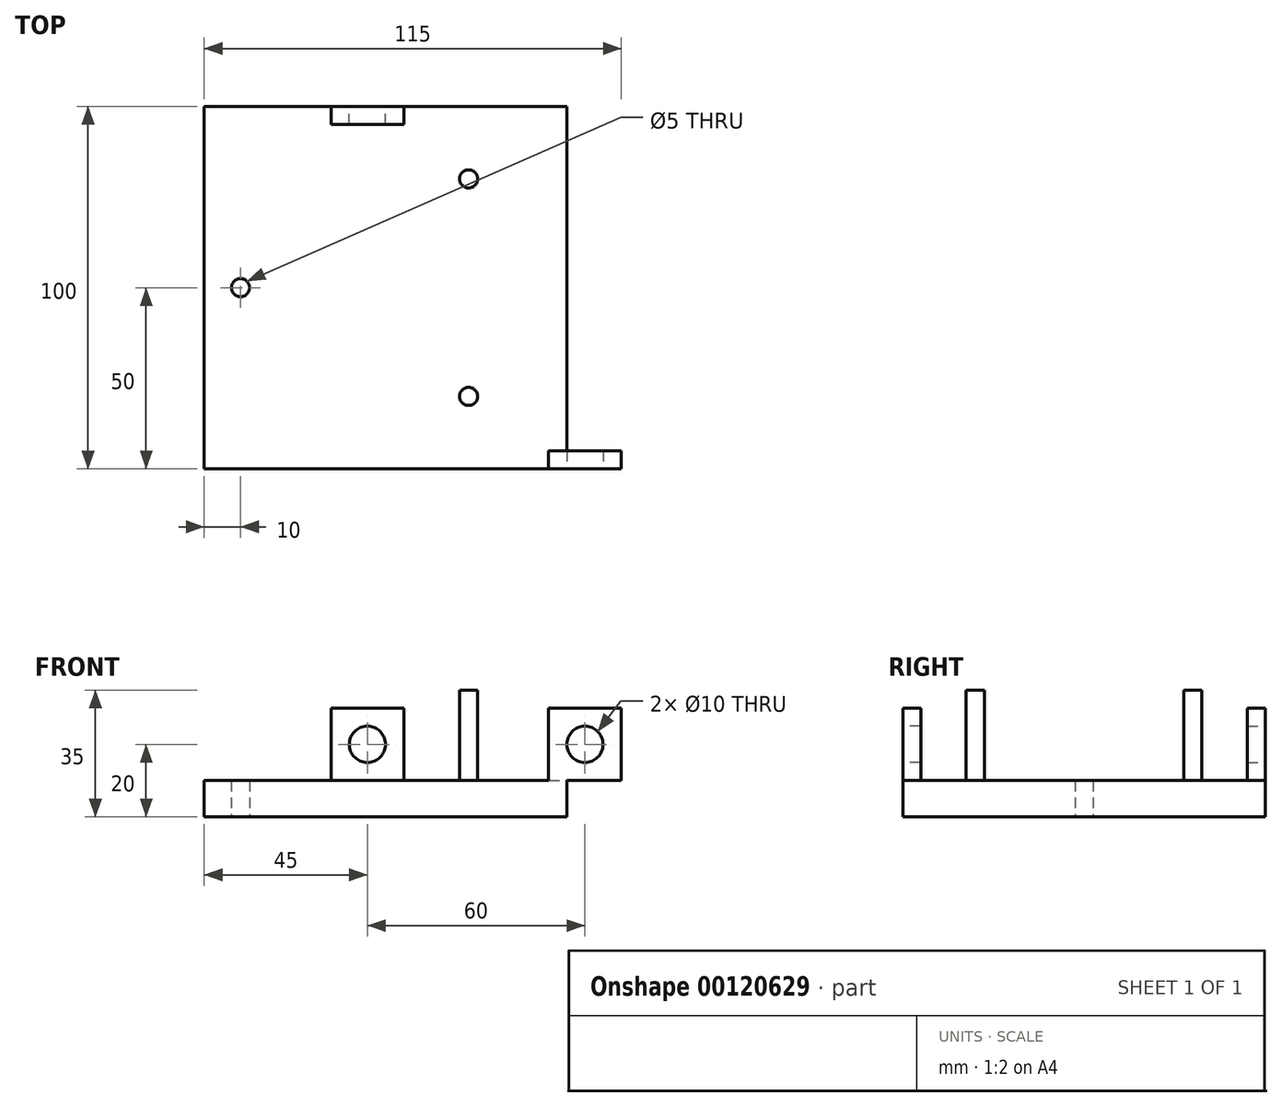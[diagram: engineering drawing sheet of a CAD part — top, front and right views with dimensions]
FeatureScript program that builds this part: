
annotation { "Feature Type Name" : "Feature", "Feature Type Description" : "" }
export const myFeature = defineFeature(function(context is Context, id is Id, definition is map)
    precondition{}
    {
        {
            var Q0;
            Q0=qCreatedBy(makeId("Top.planeOp"),FACE);
            var sketch = newSketch(context, id + "F0", { "sketchPlane" : qUnion([Q0])});
            skLineSegment(sketch, "E0.bottom", {"start": v(0, 100) * mm, "end": v(100, 100) * mm});
            skLineSegment(sketch, "E0.top", {"start": v(0, 0) * mm, "end": v(100, 0) * mm});
            skLineSegment(sketch, "E0.left", {"start": v(0, 100) * mm, "end": v(0, 0) * mm});
            skLineSegment(sketch, "E0.right", {"start": v(100, 100) * mm, "end": v(100, 0) * mm});
            skCircle(sketch, "E1", {"center": v(10, 50) * mm, "radius": 2.5 * mm});
            skSolve(sketch);
        }
        {
            var Q0;
            Q0=makeQuery(id+"F0.imprint","IMPRINT",FACE,{"disambiguationData":[TD([[makeQuery(id+"F0.imprint","IMPRINT",EDGE,{"derivedFrom":sQuery(id+"F0.wireOp",EDGE,"E0.bottom")}),-1.0]])]});
            extrude(context, id + "F1", {"entities" : qUnion([Q0]), "depth" : 10 * mm});
        }
        {
            var Q0;
            Q0=makeQuery(id+"F1.opExtrude","CAP_FACE",FACE,{"disambiguationData":[OSD([sQuery(id+"F0.wireOp",EDGE,"E0.bottom"),sQuery(id+"F0.wireOp",EDGE,"E0.top"),sQuery(id+"F0.wireOp",EDGE,"E0.left"),sQuery(id+"F0.wireOp",EDGE,"E0.right"),sQuery(id+"F0.wireOp",EDGE,"E1")])],"isStart":false});
            var sketch = newSketch(context, id + "F2", { "sketchPlane" : qUnion([Q0])});
            skCircle(sketch, "E2", {"center": v(72.91, 80) * mm, "radius": 2.5 * mm});
            skCircle(sketch, "E3", {"center": v(72.91, 20) * mm, "radius": 2.5 * mm});
            skSolve(sketch);
        }
        {
            var Q0;
            Q0=makeQuery(id+"F2.imprint","IMPRINT",FACE,{"disambiguationData":[TD([[makeQuery(id+"F2.imprint","IMPRINT",EDGE,{"derivedFrom":sQuery(id+"F2.wireOp",EDGE,"E3")}),1.0]])]});
            var Q1;
            Q1=makeQuery(id+"F2.imprint","IMPRINT",FACE,{"disambiguationData":[TD([[makeQuery(id+"F2.imprint","IMPRINT",EDGE,{"derivedFrom":sQuery(id+"F2.wireOp",EDGE,"E2")}),1.0]])]});
            extrude(context, id + "F3", {"entities" : qUnion([Q0, Q1]), "operationType" : NewBodyOperationType.ADD, "depth" : 25 * mm});
        }
        {
            var Q0;
            Q0=makeQuery(id+"F1.opExtrude","SWEPT_FACE",FACE,{"disambiguationData":[OSD([sQuery(id+"F0.wireOp",EDGE,"E0.bottom")])]});
            var sketch = newSketch(context, id + "F4", { "sketchPlane" : qUnion([Q0])});
            skLineSegment(sketch, "E4.bottom", {"start": v(-55, 10) * mm, "end": v(-35, 10) * mm});
            skLineSegment(sketch, "E4.top", {"start": v(-55, 30) * mm, "end": v(-35, 30) * mm});
            skLineSegment(sketch, "E4.left", {"start": v(-55, 10) * mm, "end": v(-55, 30) * mm});
            skLineSegment(sketch, "E4.right", {"start": v(-35, 10) * mm, "end": v(-35, 30) * mm});
            skSolve(sketch);
        }
        {
            var Q0;
            Q0=makeQuery(id+"F4.imprint","IMPRINT",FACE,{"disambiguationData":[TD([[makeQuery(id+"F4.imprint","IMPRINT",EDGE,{"derivedFrom":sQuery(id+"F4.wireOp",EDGE,"E4.bottom")}),-1.0]])]});
            extrude(context, id + "F5", {"entities" : qUnion([Q0]), "operationType" : NewBodyOperationType.ADD, "oppositeDirection" : true, "depth" : 5 * mm});
        }
        {
            var Q0;
            Q0=makeQuery(id+"F5.boolean.opBoolean","MERGE",FACE,{"derivedFrom":[makeQuery(id+"F1.opExtrude","SWEPT_FACE",FACE,{"disambiguationData":[OSD([sQuery(id+"F0.wireOp",EDGE,"E0.bottom")])]}),makeQuery(id+"F5.opExtrude","CAP_FACE",FACE,{"disambiguationData":[OSD([sQuery(id+"F4.wireOp",EDGE,"E4.bottom"),sQuery(id+"F4.wireOp",EDGE,"E4.top"),sQuery(id+"F4.wireOp",EDGE,"E4.left"),sQuery(id+"F4.wireOp",EDGE,"E4.right")])],"isStart":true})]});
            var sketch = newSketch(context, id + "F6", { "sketchPlane" : qUnion([Q0])});
            skCircle(sketch, "E5", {"center": v(-45, 20) * mm, "radius": 5 * mm});
            skSolve(sketch);
        }
        {
            var Q0;
            Q0=makeQuery(id+"F6.imprint","IMPRINT",FACE,{"disambiguationData":[TD([[makeQuery(id+"F6.imprint","IMPRINT",EDGE,{"derivedFrom":sQuery(id+"F6.wireOp",EDGE,"E5")}),1.0]])]});
            extrude(context, id + "F7", {"entities" : qUnion([Q0]), "operationType" : NewBodyOperationType.REMOVE, "oppositeDirection" : true, "depth" : 25 * mm});
        }
        {
            var Q0;
            Q0=makeQuery(id+"F1.opExtrude","SWEPT_FACE",FACE,{"disambiguationData":[OSD([sQuery(id+"F0.wireOp",EDGE,"E0.top")])]});
            var sketch = newSketch(context, id + "F8", { "sketchPlane" : qUnion([Q0])});
            skLineSegment(sketch, "E6.bottom", {"start": v(95, 10) * mm, "end": v(115, 10) * mm});
            skLineSegment(sketch, "E6.top", {"start": v(95, 30) * mm, "end": v(115, 30) * mm});
            skLineSegment(sketch, "E6.left", {"start": v(95, 10) * mm, "end": v(95, 30) * mm});
            skLineSegment(sketch, "E6.right", {"start": v(115, 10) * mm, "end": v(115, 30) * mm});
            skCircle(sketch, "E7", {"center": v(105, 20) * mm, "radius": 5 * mm});
            skSolve(sketch);
        }
        {
            var Q0;
            Q0=makeQuery(id+"F8.imprint","IMPRINT",FACE,{"disambiguationData":[TD([[makeQuery(id+"F8.imprint","IMPRINT",EDGE,{"derivedFrom":sQuery(id+"F8.wireOp",EDGE,"E6.top")}),-1.0]])]});
            extrude(context, id + "F9", {"entities" : qUnion([Q0]), "operationType" : NewBodyOperationType.ADD, "oppositeDirection" : true, "depth" : 5 * mm});
        }
    });
